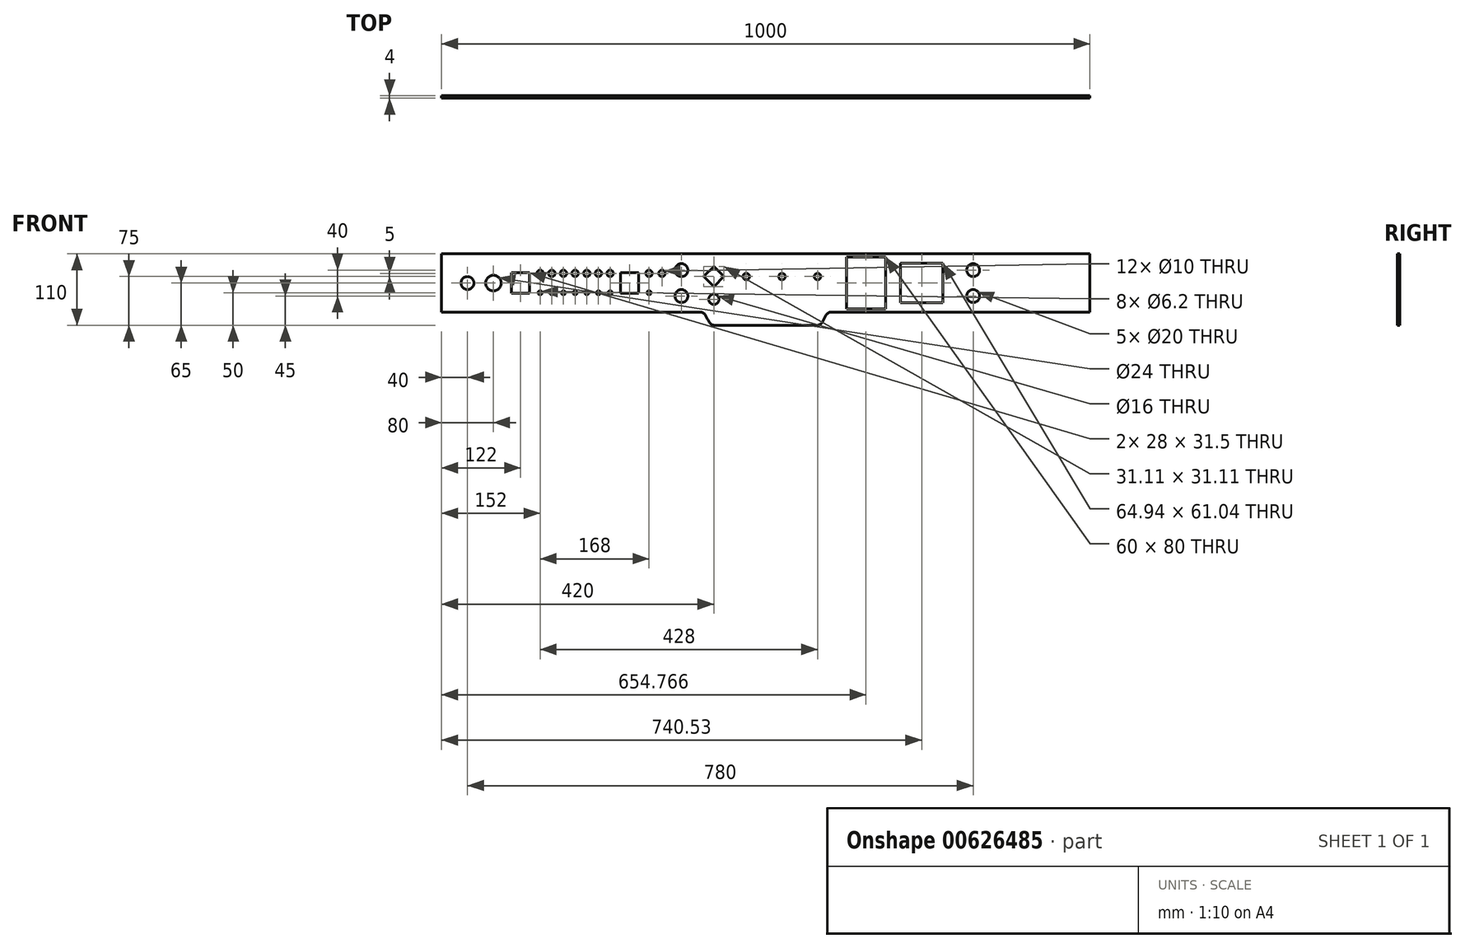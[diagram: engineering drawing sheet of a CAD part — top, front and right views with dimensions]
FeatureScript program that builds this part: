
annotation { "Feature Type Name" : "Feature", "Feature Type Description" : "" }
export const myFeature = defineFeature(function(context is Context, id is Id, definition is map)
    precondition{}
    {
        {
            var Q0;
            Q0=qCreatedBy(makeId("Front.planeOp"),FACE);
            var sketch = newSketch(context, id + "F0", { "sketchPlane" : qUnion([Q0])});
            skLineSegment(sketch, "E0.bottom", {"start": v(-500, 90) * mm, "end": v(500, 90) * mm});
            skLineSegment(sketch, "E0.top", {"start": v(-500, 0) * mm, "end": v(500, 0) * mm});
            skLineSegment(sketch, "E0.left", {"start": v(-500, 90) * mm, "end": v(-500, 0) * mm});
            skLineSegment(sketch, "E0.right", {"start": v(500, 90) * mm, "end": v(500, 0) * mm});
            skCircle(sketch, "E1", {"center": v(-420, 45) * mm, "radius": 12 * mm});
            skLineSegment(sketch, "E2.bottom", {"start": v(-392, 60.75) * mm, "end": v(-378, 60.75) * mm});
            skLineSegment(sketch, "E2.top", {"start": v(-392, 29.25) * mm, "end": v(-378, 29.25) * mm});
            skLineSegment(sketch, "E2.left", {"start": v(-392, 60.75) * mm, "end": v(-392, 29.25) * mm});
            skLineSegment(sketch, "E2.right", {"start": v(-378, 60.75) * mm, "end": v(-378, 29.25) * mm});
            skLineSegment(sketch, "E3.bottom", {"start": v(-378, 60.75) * mm, "end": v(-364, 60.75) * mm});
            skLineSegment(sketch, "E3.top", {"start": v(-378, 29.25) * mm, "end": v(-364, 29.25) * mm});
            skLineSegment(sketch, "E3.right", {"start": v(-364, 60.75) * mm, "end": v(-364, 29.25) * mm});
            skCircle(sketch, "E4", {"center": v(-348, 30) * mm, "radius": 3.1 * mm});
            skCircle(sketch, "E5", {"center": v(-330, 30) * mm, "radius": 3.1 * mm});
            skCircle(sketch, "E6", {"center": v(-312, 30) * mm, "radius": 3.1 * mm});
            skCircle(sketch, "E7", {"center": v(-294, 30) * mm, "radius": 3.1 * mm});
            skCircle(sketch, "E8", {"center": v(-276, 30) * mm, "radius": 3.1 * mm});
            skCircle(sketch, "E9", {"center": v(-258, 30) * mm, "radius": 3.1 * mm});
            skCircle(sketch, "E10", {"center": v(-240, 30) * mm, "radius": 3.1 * mm});
            skLineSegment(sketch, "E11.bottom", {"start": v(-224, 60.75) * mm, "end": v(-210, 60.75) * mm});
            skLineSegment(sketch, "E11.top", {"start": v(-224, 29.25) * mm, "end": v(-210, 29.25) * mm});
            skLineSegment(sketch, "E11.left", {"start": v(-224, 60.75) * mm, "end": v(-224, 29.25) * mm});
            skLineSegment(sketch, "E11.right", {"start": v(-210, 60.75) * mm, "end": v(-210, 29.25) * mm});
            skLineSegment(sketch, "E12.bottom", {"start": v(-210, 60.75) * mm, "end": v(-196, 60.75) * mm});
            skLineSegment(sketch, "E12.top", {"start": v(-210, 29.25) * mm, "end": v(-196, 29.25) * mm});
            skLineSegment(sketch, "E12.right", {"start": v(-196, 60.75) * mm, "end": v(-196, 29.25) * mm});
            skLineSegment(sketch, "E13", {"start": v(-80, -20) * mm, "end": v(80, -20) * mm});
            skPoint(sketch, "E14", {"position": v(-100, 0) * mm});
            skFitSpline(sketch, "E15", {"points": [v(-100, 0) * mm, v(-80, -20) * mm], "startDerivative": vector(30, 0) * mm, "endDerivative": vector(30, 0) * mm});
            skFitSpline(sketch, "E16.MirrorCS", {"points": [v(100, 0) * mm, v(80, -20) * mm], "startDerivative": vector(-30, 0) * mm, "endDerivative": vector(-30, 0) * mm});
            skCircle(sketch, "E17", {"center": v(-460, 45) * mm, "radius": 10 * mm});
            skCircle(sketch, "E18", {"center": v(-30, 55) * mm, "radius": 5 * mm});
            skCircle(sketch, "E19", {"center": v(25, 55) * mm, "radius": 5 * mm});
            skCircle(sketch, "E20", {"center": v(80, 55) * mm, "radius": 5 * mm});
            skCircle(sketch, "E21", {"center": v(-80, 20) * mm, "radius": 8 * mm});
            skCircle(sketch, "E22", {"center": v(-130, 65) * mm, "radius": 10 * mm});
            skCircle(sketch, "E23", {"center": v(-130, 25) * mm, "radius": 10 * mm});
            skCircle(sketch, "E24", {"center": v(-180, 30) * mm, "radius": 3.1 * mm});
            skLineSegment(sketch, "E25.bottom", {"start": v(124.77, 85) * mm, "end": v(184.77, 85) * mm});
            skLineSegment(sketch, "E25.top", {"start": v(124.77, 5) * mm, "end": v(184.77, 5) * mm});
            skLineSegment(sketch, "E25.left", {"start": v(124.77, 85) * mm, "end": v(124.77, 5) * mm});
            skLineSegment(sketch, "E25.right", {"start": v(184.77, 85) * mm, "end": v(184.77, 5) * mm});
            skLineSegment(sketch, "E26.bottom", {"start": v(208.06, 75.52) * mm, "end": v(273, 75.52) * mm});
            skLineSegment(sketch, "E26.top", {"start": v(208.06, 14.48) * mm, "end": v(273, 14.48) * mm});
            skLineSegment(sketch, "E26.left", {"start": v(208.06, 75.52) * mm, "end": v(208.06, 14.48) * mm});
            skLineSegment(sketch, "E26.right", {"start": v(273, 75.52) * mm, "end": v(273, 14.48) * mm});
            skCircle(sketch, "E27", {"center": v(320, 65) * mm, "radius": 10 * mm});
            skCircle(sketch, "E28", {"center": v(320, 25) * mm, "radius": 10 * mm});
            skCircle(sketch, "E29", {"center": v(-348, 60) * mm, "radius": 5 * mm});
            skCircle(sketch, "E30", {"center": v(-330, 60) * mm, "radius": 5 * mm});
            skCircle(sketch, "E31", {"center": v(-312, 60) * mm, "radius": 5 * mm});
            skCircle(sketch, "E32", {"center": v(-294, 60) * mm, "radius": 5 * mm});
            skCircle(sketch, "E33", {"center": v(-276, 60) * mm, "radius": 5 * mm});
            skCircle(sketch, "E34", {"center": v(-258, 60) * mm, "radius": 5 * mm});
            skCircle(sketch, "E35", {"center": v(-240, 60) * mm, "radius": 5 * mm});
            skLineSegment(sketch, "E36", {"start": v(-100, 90) * mm, "end": v(-100, 0) * mm, "construction": true});
            skLineSegment(sketch, "E37.MirrorCS", {"start": v(100, 90) * mm, "end": v(100, 0) * mm, "construction": true});
            skCircle(sketch, "E38", {"center": v(-180, 60) * mm, "radius": 5 * mm});
            skCircle(sketch, "E39", {"center": v(-160, 60) * mm, "radius": 5 * mm});
            skCircle(sketch, "E40.cCircle", {"center": v(-80, 55) * mm, "radius": 11 * mm, "construction": true});
            skLineSegment(sketch, "E40.0", {"start": v(-80, 70.56) * mm, "end": v(-95.56, 55) * mm});
            skLineSegment(sketch, "E40.1", {"start": v(-64.44, 55) * mm, "end": v(-80, 70.56) * mm});
            skLineSegment(sketch, "E40.2", {"start": v(-80, 39.44) * mm, "end": v(-64.44, 55) * mm});
            skLineSegment(sketch, "E40.3", {"start": v(-95.56, 55) * mm, "end": v(-80, 39.44) * mm});
            skPoint(sketch, "E40.0.midPoint", {"position": v(-87.78, 62.78) * mm});
            skCircle(sketch, "E41", {"center": v(-80, 55) * mm, "radius": 7 * mm});
            skPoint(sketch, "E42", {"position": v(-500, 45) * mm});
            skPoint(sketch, "E43", {"position": v(-378, 45) * mm});
            skPoint(sketch, "E44", {"position": v(-210, 45) * mm});
            skCircle(sketch, "E45", {"center": v(-80, 20) * mm, "radius": 4.5 * mm});
            skCircle(sketch, "E46", {"center": v(-130, 25) * mm, "radius": 6 * mm});
            skCircle(sketch, "E47", {"center": v(-130, 65) * mm, "radius": 6 * mm});
            skCircle(sketch, "E48", {"center": v(320, 65) * mm, "radius": 6 * mm});
            skCircle(sketch, "E49", {"center": v(320, 25) * mm, "radius": 6 * mm});
            skCircle(sketch, "E50", {"center": v(-420, 45) * mm, "radius": 7 * mm});
            skLineSegment(sketch, "E51", {"start": v(154.77, 85) * mm, "end": v(154.77, 5) * mm, "construction": true});
            skLineSegment(sketch, "E52", {"start": v(240.53, 75.52) * mm, "end": v(240.53, 14.48) * mm, "construction": true});
            skPoint(sketch, "E53", {"position": v(154.77, 45) * mm});
            skPoint(sketch, "E54", {"position": v(240.53, 45) * mm});
            skPoint(sketch, "E55", {"position": v(500, 45) * mm});
            skSolve(sketch);
        }
        {
            var Q0;
            Q0 = qSketchRegion(id + "F0", true);
            extrude(context, id + "F1", {"entities" : qUnion([Q0]), "depth" : 4 * mm, "offsetDistance" : 25 * mm});
        }
    });
